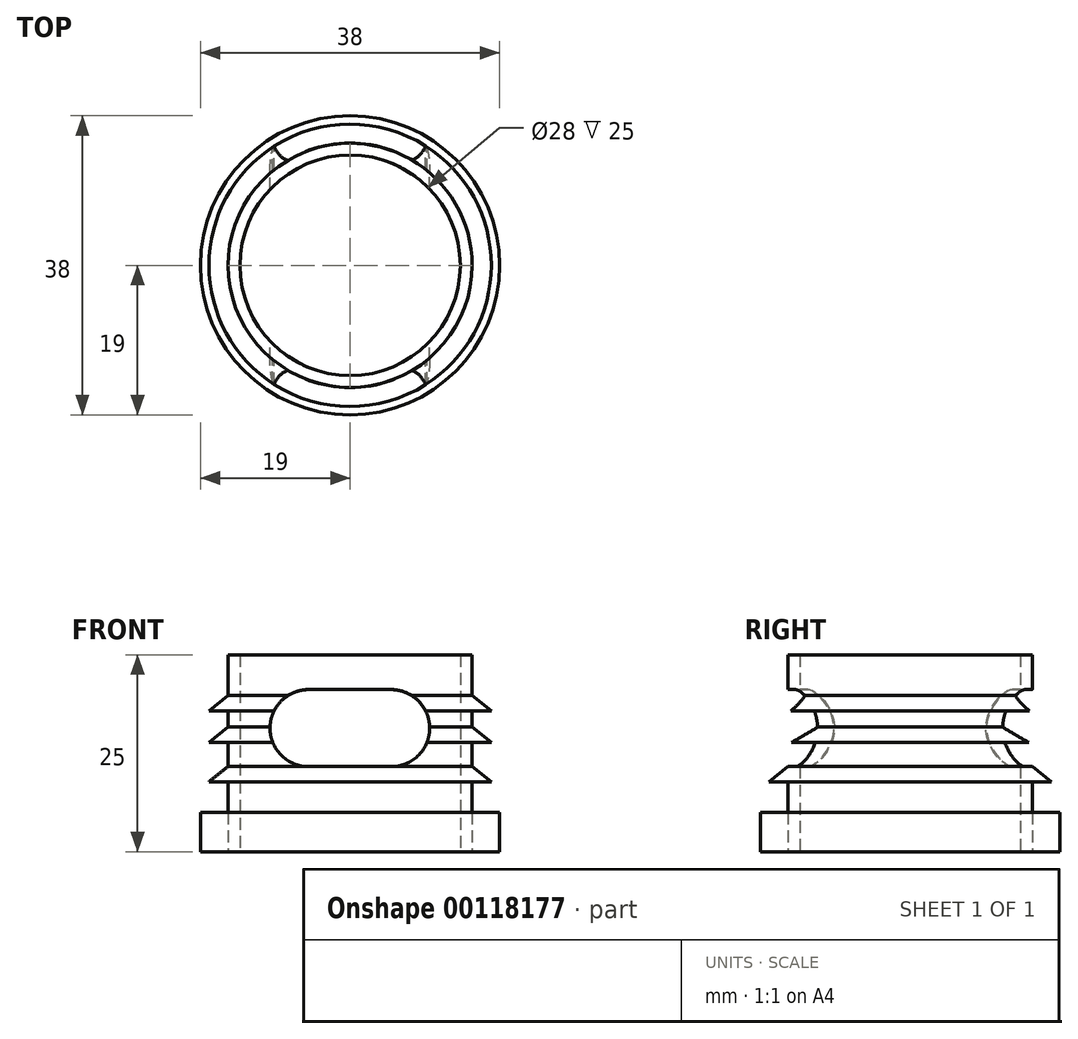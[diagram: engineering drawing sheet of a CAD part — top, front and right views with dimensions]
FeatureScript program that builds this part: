
annotation { "Feature Type Name" : "Feature", "Feature Type Description" : "" }
export const myFeature = defineFeature(function(context is Context, id is Id, definition is map)
    precondition{}
    {
        {
            var Q0;
            Q0=qCreatedBy(makeId("Top.planeOp"),FACE);
            var sketch = newSketch(context, id + "F0", { "sketchPlane" : qUnion([Q0])});
            skCircle(sketch, "E0", {"center": v(0, 0) * mm, "radius": 19 * mm});
            skCircle(sketch, "E1", {"center": v(0, 0) * mm, "radius": 15.5 * mm});
            skCircle(sketch, "E2.0", {"center": v(0, 0) * mm, "radius": 14 * mm});
            skSolve(sketch);
        }
        {
            var Q0;
            Q0=makeQuery(id+"F0.imprint","IMPRINT",FACE,{"disambiguationData":[TD([[makeQuery(id+"F0.imprint","IMPRINT",EDGE,{"derivedFrom":sQuery(id+"F0.wireOp",EDGE,"E2.0")}),1.0]])]});
            var Q1;
            Q1=makeQuery(id+"F0.imprint","IMPRINT",FACE,{"disambiguationData":[TD([[makeQuery(id+"F0.imprint","IMPRINT",EDGE,{"derivedFrom":sQuery(id+"F0.wireOp",EDGE,"E0")}),1.0]])]});
            var Q2;
            Q2=makeQuery(id+"F0.imprint","IMPRINT",FACE,{"disambiguationData":[TD([[makeQuery(id+"F0.imprint","IMPRINT",EDGE,{"derivedFrom":sQuery(id+"F0.wireOp",EDGE,"E1")}),1.0]])]});
            extrude(context, id + "F1", {"entities" : qUnion([Q0, Q1, Q2]), "depth" : 5 * mm});
        }
        {
            var Q0;
            Q0=makeQuery(id+"F0.imprint","IMPRINT",FACE,{"disambiguationData":[TD([[makeQuery(id+"F0.imprint","IMPRINT",EDGE,{"derivedFrom":sQuery(id+"F0.wireOp",EDGE,"E1")}),1.0]])]});
            extrude(context, id + "F2", {"entities" : qUnion([Q0]), "depth" : 25 * mm});
        }
        {
            var Q0;
            Q0=qCreatedBy(makeId("Front.planeOp"),FACE);
            var sketch = newSketch(context, id + "F3", { "sketchPlane" : qUnion([Q0])});
            skLineSegment(sketch, "E3", {"start": v(15.44, 19.89) * mm, "end": v(15.44, 17.89) * mm});
            skLineSegment(sketch, "E4", {"start": v(15.44, 17.89) * mm, "end": v(17.94, 17.89) * mm});
            skLineSegment(sketch, "E5", {"start": v(17.94, 17.89) * mm, "end": v(15.44, 19.89) * mm});
            skLineSegment(sketch, "E6", {"start": v(15.44, 15.89) * mm, "end": v(15.44, 13.89) * mm});
            skLineSegment(sketch, "E7", {"start": v(15.44, 13.89) * mm, "end": v(17.94, 13.89) * mm});
            skLineSegment(sketch, "E8", {"start": v(17.94, 13.89) * mm, "end": v(15.44, 15.89) * mm});
            skLineSegment(sketch, "E9", {"start": v(15.44, 10.89) * mm, "end": v(15.44, 8.89) * mm});
            skLineSegment(sketch, "E10", {"start": v(15.44, 8.89) * mm, "end": v(17.94, 8.89) * mm});
            skLineSegment(sketch, "E11", {"start": v(17.94, 8.89) * mm, "end": v(15.44, 10.89) * mm});
            skLineSegment(sketch, "E12", {"start": v(0, 0) * mm, "end": v(0, 37.43) * mm});
            skSolve(sketch);
        }
        {
            var Q0;
            Q0=makeQuery(id+"F3.imprint","IMPRINT",FACE,{"disambiguationData":[TD([[makeQuery(id+"F3.imprint","IMPRINT",EDGE,{"derivedFrom":sQuery(id+"F3.wireOp",EDGE,"E6")}),1.0]])]});
            var Q1;
            Q1=makeQuery(id+"F3.imprint","IMPRINT",FACE,{"disambiguationData":[TD([[makeQuery(id+"F3.imprint","IMPRINT",EDGE,{"derivedFrom":sQuery(id+"F3.wireOp",EDGE,"E3")}),1.0]])]});
            var Q2;
            Q2=makeQuery(id+"F3.imprint","IMPRINT",FACE,{"disambiguationData":[TD([[makeQuery(id+"F3.imprint","IMPRINT",EDGE,{"derivedFrom":sQuery(id+"F3.wireOp",EDGE,"E9")}),1.0]])]});
            var Q3;
            Q3=sQuery(id+"F3.wireOp",EDGE,"E12");
            revolve(context, id + "F4", {"operationType" : NewBodyOperationType.ADD, "entities" : qUnion([Q0, Q1, Q2]), "axis" : qUnion([Q3]), "revolveType" : RevolveType.FULL});
        }
        {
            var Q0;
            Q0=qCreatedBy(makeId("Front.planeOp"),FACE);
            var sketch = newSketch(context, id + "F5", { "sketchPlane" : qUnion([Q0])});
            skCircle(sketch, "E13", {"center": v(-5.28, 15.7) * mm, "radius": 4.9 * mm});
            skCircle(sketch, "E14", {"center": v(5.2, 15.7) * mm, "radius": 4.9 * mm});
            skLineSegment(sketch, "E15", {"start": v(-5.28, 10.81) * mm, "end": v(5.2, 10.81) * mm});
            skLineSegment(sketch, "E16", {"start": v(-5.28, 20.6) * mm, "end": v(5.2, 20.6) * mm});
            skSolve(sketch);
        }
        {
            var Q0;
            {var subQ0=sQuery(id+"F5.wireOp",EDGE,"E13");var subQ1=makeQuery(id+"F5.imprint","INTERSECT",VERTEX,{"derivedFrom":[subQ0,sQuery(id+"F5.wireOp",EDGE,"E15")]});Q0=makeQuery(id+"F5.imprint","IMPRINT",FACE,{"disambiguationData":[TD([[makeQuery(id+"F5.imprint","IMPRINT",EDGE,{"disambiguationData":[TD([[subQ1,1.0]])],"derivedFrom":subQ0}),1.0]])]});}
            var Q1;
            {var subQ0=sQuery(id+"F5.wireOp",EDGE,"E14");var subQ1=makeQuery(id+"F5.imprint","INTERSECT",VERTEX,{"derivedFrom":[subQ0,sQuery(id+"F5.wireOp",EDGE,"E15")]});Q1=makeQuery(id+"F5.imprint","IMPRINT",FACE,{"disambiguationData":[TD([[makeQuery(id+"F5.imprint","IMPRINT",EDGE,{"disambiguationData":[TD([[subQ1,1.0]])],"derivedFrom":subQ0}),1.0]])]});}
            var Q2;
            {var subQ0=sQuery(id+"F5.wireOp",EDGE,"E15");Q2=makeQuery(id+"F5.imprint","IMPRINT",FACE,{"disambiguationData":[TD([[makeQuery(id+"F5.imprint","IMPRINT",EDGE,{"derivedFrom":subQ0}),1.0]])]});}
            extrude(context, id + "F6", {"entities" : qUnion([Q0, Q1, Q2]), "endBound" : BoundingType.SYMMETRIC, "depth" : 50 * mm});
        }
        {
            var Q0;
            Q0=makeQuery(id+"F6.opExtrude","SWEPT_BODY",BODY,{"disambiguationData":[OSD([sQuery(id+"F5.wireOp",EDGE,"E13"),sQuery(id+"F5.wireOp",EDGE,"E14"),sQuery(id+"F5.wireOp",EDGE,"E15"),sQuery(id+"F5.wireOp",EDGE,"E16")])]});
            var Q1;
            Q1=makeQuery(id+"F2.opExtrude","SWEPT_BODY",BODY,{"disambiguationData":[OSD([sQuery(id+"F0.wireOp",EDGE,"E1"),sQuery(id+"F0.wireOp",EDGE,"E2.0")])]});
            booleanBodies(context, id + "F7", {"operationType" : BooleanOperationType.SUBTRACTION, "tools" : qUnion([Q0]), "targets" : qUnion([Q1])});
        }
    });
